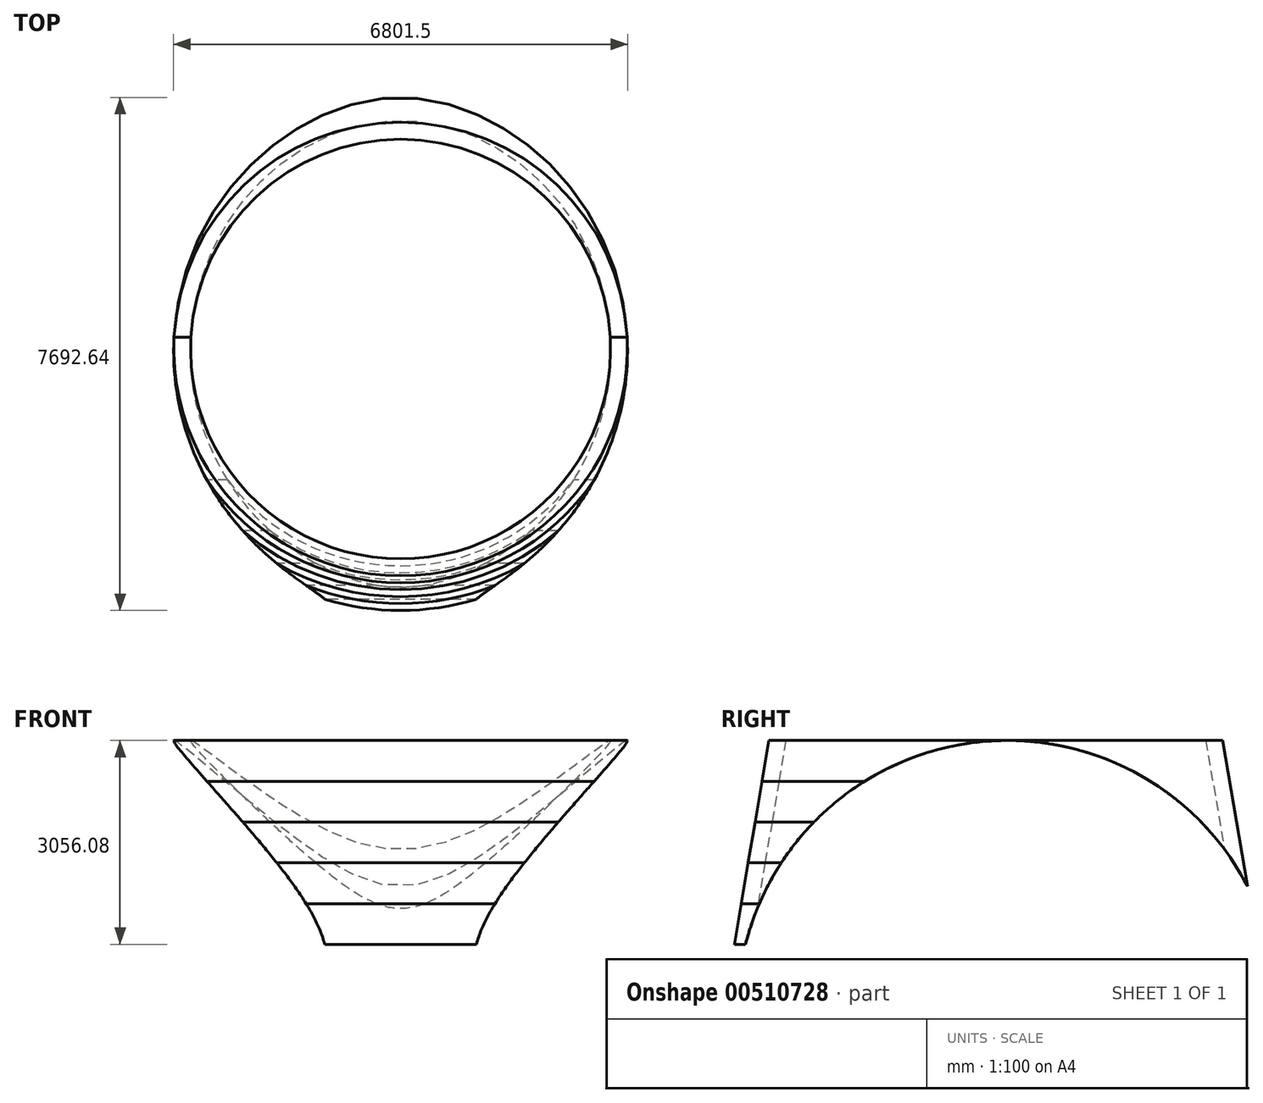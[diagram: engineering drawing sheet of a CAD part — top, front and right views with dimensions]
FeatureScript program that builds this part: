
annotation { "Feature Type Name" : "Feature", "Feature Type Description" : "" }
export const myFeature = defineFeature(function(context is Context, id is Id, definition is map)
    precondition{}
    {
        {
            var Q0;
            Q0=qCreatedBy(makeId("Right.planeOp"),FACE);
            var sketch = newSketch(context, id + "F0", { "sketchPlane" : qUnion([Q0])});
            skLineSegment(sketch, "E0", {"start": v(-3146.4, 1538.32) * mm, "end": v(-3666.4, -1517.76) * mm});
            skLineSegment(sketch, "E1", {"start": v(-3920, -1517.76) * mm, "end": v(-3666.4, -1517.76) * mm});
            skLineSegment(sketch, "E2", {"start": v(-3920, -1517.76) * mm, "end": v(-3400, 1538.32) * mm});
            skLineSegment(sketch, "E3", {"start": v(-3146.4, 1538.32) * mm, "end": v(-3400, 1538.32) * mm});
            skLineSegment(sketch, "E4", {"start": v(0, -1209.26) * mm, "end": v(0, 2251.84) * mm});
            skSolve(sketch);
        }
        {
            var Q0;
            Q0=makeQuery(id+"F0.imprint","IMPRINT",FACE,{"disambiguationData":[TD([[makeQuery(id+"F0.imprint","IMPRINT",EDGE,{"derivedFrom":sQuery(id+"F0.wireOp",EDGE,"E0")}),-1.0]])]});
            var Q1;
            Q1=sQuery(id+"F0.wireOp",EDGE,"E4");
            revolve(context, id + "F1", {"entities" : qUnion([Q0]), "axis" : qUnion([Q1]), "revolveType" : RevolveType.FULL});
        }
        {
            var Q0;
            Q0=qCreatedBy(makeId("Right.planeOp"),FACE);
            var sketch = newSketch(context, id + "F2", { "sketchPlane" : qUnion([Q0])});
            skCircle(sketch, "E5", {"center": v(175, -2511.68) * mm, "radius": 4050 * mm});
            skSolve(sketch);
        }
        {
            var Q0;
            Q0 = qSketchRegion(id + "F2", true);
            extrude(context, id + "F3", {"entities" : qUnion([Q0]), "operationType" : NewBodyOperationType.REMOVE, "endBound" : BoundingType.SYMMETRIC, "depth" : 10000 * mm});
        }
        {
            var Q0;
            Q0=makeQuery(id+"F3.boolean.opBoolean","SPLIT",FACE,{"disambiguationData":[OD(1.0)],"derivedFrom":makeQuery(id+"F1.opRevolve","SWEPT_FACE",FACE,{"disambiguationData":[OSD([sQuery(id+"F0.wireOp",EDGE,"E3")])]})});
            cPlane(context, id + "F4", {"entities" : qUnion([Q0]), "cplaneType" : CPlaneType.OFFSET, "offset" : 611.2 * mm, "oppositeDirection" : true, "width" : 150 * mm, "height" : 150 * mm});
        }
        {
            var Q0;
            Q0=qCreatedBy(id+"F4.planeOp",FACE);
            cPlane(context, id + "F5", {"entities" : qUnion([Q0]), "cplaneType" : CPlaneType.OFFSET, "offset" : 611.2 * mm, "oppositeDirection" : true, "width" : 150 * mm, "height" : 150 * mm});
        }
        {
            var Q0;
            Q0=qCreatedBy(id+"F5.planeOp",FACE);
            cPlane(context, id + "F6", {"entities" : qUnion([Q0]), "cplaneType" : CPlaneType.OFFSET, "offset" : 611.2 * mm, "oppositeDirection" : true, "width" : 150 * mm, "height" : 150 * mm});
        }
        {
            var Q0;
            Q0=qCreatedBy(makeId("Right.planeOp"),FACE);
            var sketch = newSketch(context, id + "F7", { "sketchPlane" : qUnion([Q0])});
            skLineSegment(sketch, "E6.bottom", {"start": v(-10000, 927.12) * mm, "end": v(0, 927.12) * mm});
            skLineSegment(sketch, "E6.top", {"start": v(-10000, 927.11) * mm, "end": v(0, 927.11) * mm});
            skLineSegment(sketch, "E6.left", {"start": v(-10000, 927.12) * mm, "end": v(-10000, 927.11) * mm});
            skLineSegment(sketch, "E6.right", {"start": v(0, 927.12) * mm, "end": v(0, 927.11) * mm});
            skLineSegment(sketch, "E7.bottom", {"start": v(-10000, 313.92) * mm, "end": v(0, 313.92) * mm});
            skLineSegment(sketch, "E7.top", {"start": v(-10000, 313.91) * mm, "end": v(0, 313.91) * mm});
            skLineSegment(sketch, "E7.left", {"start": v(-10000, 313.92) * mm, "end": v(-10000, 313.91) * mm});
            skLineSegment(sketch, "E7.right", {"start": v(0, 313.92) * mm, "end": v(0, 313.91) * mm});
            skLineSegment(sketch, "E8.bottom", {"start": v(-10000, -297.28) * mm, "end": v(0, -297.28) * mm});
            skLineSegment(sketch, "E8.top", {"start": v(-10000, -297.29) * mm, "end": v(0, -297.29) * mm});
            skLineSegment(sketch, "E8.left", {"start": v(-10000, -297.28) * mm, "end": v(-10000, -297.29) * mm});
            skLineSegment(sketch, "E8.right", {"start": v(0, -297.28) * mm, "end": v(0, -297.29) * mm});
            skLineSegment(sketch, "E9.bottom", {"start": v(-10000, -908.48) * mm, "end": v(0, -908.48) * mm});
            skLineSegment(sketch, "E9.top", {"start": v(-10000, -908.49) * mm, "end": v(0, -908.49) * mm});
            skLineSegment(sketch, "E9.left", {"start": v(-10000, -908.48) * mm, "end": v(-10000, -908.49) * mm});
            skLineSegment(sketch, "E9.right", {"start": v(0, -908.48) * mm, "end": v(0, -908.49) * mm});
            skSolve(sketch);
        }
        {
            var Q0;
            Q0 = qSketchRegion(id + "F7", true);
            extrude(context, id + "F8", {"entities" : qUnion([Q0]), "operationType" : NewBodyOperationType.REMOVE, "endBound" : BoundingType.SYMMETRIC, "oppositeDirection" : true, "depth" : 10000 * mm});
        }
    });
